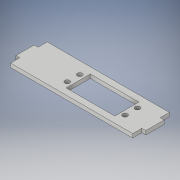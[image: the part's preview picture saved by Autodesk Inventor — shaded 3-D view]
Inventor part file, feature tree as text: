
AUTODESK INVENTOR PART (.ipt)
format: ipt  version: 2019 (Build 230136000, 136)  size: 134,656 bytes
history: native  units: mm
features: other x1, extrude x1, sketch x1
ambient origin geometry x8: Origin, YZ Plane, XZ Plane, XY Plane, X Axis, Y Axis, Z Axis, Center Point
bodies: Body1 (feature_tree)
feature tree (3):
  other  "Sólido1"
  extrude  "Extrusión1"  Depth=3.18mm
  sketch  "Boceto2"  dims[d2=10.0mm d3=9.91mm d4=19.82mm d5=9.66mm d6=39.88mm d7=4.0mm d8=4.0mm d9=4.0mm d10=5.085mm d11=10.17mm d12=13.47mm d13=13.47mm d14=4.0mm d15=33.79mm d16=33.79mm d17=5.085mm d18=10.17mm d19=100.0mm d20=30.0mm d21=3.18mm d22=15.0mm d23=7.5mm d24=15.0mm d25=3.18mm d26=7.5mm d27=3.18mm d28=0.0mm]
